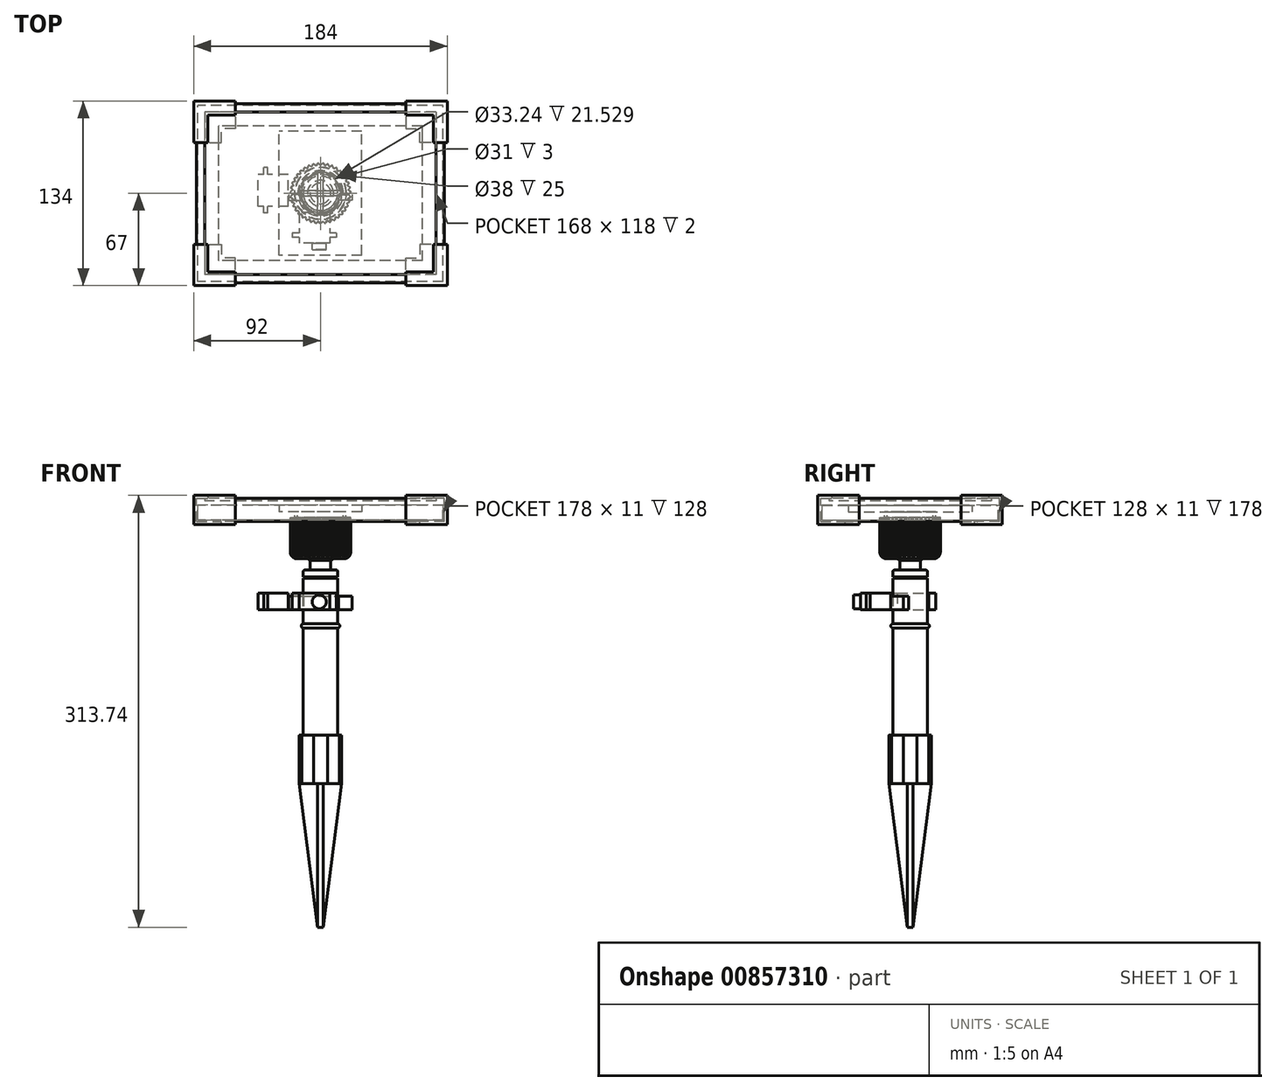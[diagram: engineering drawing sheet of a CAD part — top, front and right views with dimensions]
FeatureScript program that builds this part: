
annotation { "Feature Type Name" : "Feature", "Feature Type Description" : "" }
export const myFeature = defineFeature(function(context is Context, id is Id, definition is map)
    precondition{}
    {
        {
            var Q0;
            Q0=qCreatedBy(makeId("Front.planeOp"),FACE);
            var sketch = newSketch(context, id + "F0", { "sketchPlane" : qUnion([Q0])});
            skArc(sketch, "E0", {"start": v(7.5, 35.85) * mm, "mid": v(14.49, 52.72) * mm, "end": v(0, 63.84) * mm});
            skLineSegment(sketch, "E1", {"start": v(7.5, 35.85) * mm, "end": v(7.5, 28.85) * mm});
            skLineSegment(sketch, "E2", {"start": v(7.5, 28.85) * mm, "end": v(12.5, 28.85) * mm});
            skLineSegment(sketch, "E3", {"start": v(12.5, 28.85) * mm, "end": v(12.5, 23.85) * mm});
            skLineSegment(sketch, "E4", {"start": v(12.5, 23.85) * mm, "end": v(9.5, 23.85) * mm});
            skLineSegment(sketch, "E5", {"start": v(9.5, 23.85) * mm, "end": v(9.5, 22.85) * mm});
            skLineSegment(sketch, "E6", {"start": v(9.5, 22.85) * mm, "end": v(12.5, 22.85) * mm});
            skLineSegment(sketch, "E7", {"start": v(12.5, 22.85) * mm, "end": v(12.5, -10.15) * mm});
            skLineSegment(sketch, "E8", {"start": v(0, -126.15) * mm, "end": v(0, 63.84) * mm});
            skLineSegment(sketch, "E9", {"start": v(12.5, -91.15) * mm, "end": v(14.5, -91.15) * mm});
            skLineSegment(sketch, "E10", {"start": v(14.5, -91.15) * mm, "end": v(14.5, -126.15) * mm});
            skLineSegment(sketch, "E11", {"start": v(14.5, -126.15) * mm, "end": v(0, -126.15) * mm});
            skPoint(sketch, "E12.orphan", {"position": v(0, -41.58) * mm});
            skArc(sketch, "E13", {"start": v(12.5, -13.15) * mm, "mid": v(14, -11.65) * mm, "end": v(12.5, -10.15) * mm});
            skLineSegment(sketch, "E14.trimOffspring", {"start": v(12.5, -13.15) * mm, "end": v(12.5, -91.15) * mm});
            skSolve(sketch);
        }
        {
            var Q0;
            Q0=makeQuery(id+"F0.imprint","IMPRINT",FACE,{"disambiguationData":[TD([[makeQuery(id+"F0.imprint","IMPRINT",EDGE,{"derivedFrom":sQuery(id+"F0.wireOp",EDGE,"E0")}),1.0]])]});
            var Q1;
            Q1=sQuery(id+"F0.wireOp",EDGE,"E8");
            revolve(context, id + "F1", {"surfaceOperationType" : NewSurfaceOperationType.NEW, "entities" : qUnion([Q0]), "axis" : qUnion([Q1]), "revolveType" : RevolveType.FULL});
        }
        {
            var Q0;
            Q0=makeQuery(id+"F1.opRevolve","SWEPT_FACE",FACE,{"disambiguationData":[OSD([sQuery(id+"F0.wireOp",EDGE,"E9")])]});
            var sketch = newSketch(context, id + "F2", { "sketchPlane" : qUnion([Q0])});
            skArc(sketch, "E15", {"start": v(5, 14.61) * mm, "mid": v(0, 15.44) * mm, "end": v(-5, 14.61) * mm});
            skArc(sketch, "E16", {"start": v(5, 13.61) * mm, "mid": v(0, 14.5) * mm, "end": v(-5, 13.61) * mm});
            skLineSegment(sketch, "E17", {"start": v(5, 14.61) * mm, "end": v(5, 13.61) * mm});
            skLineSegment(sketch, "E18.MirrorCS", {"start": v(-5, 14.61) * mm, "end": v(-5, 13.61) * mm});
            skArc(sketch, "E19.1.0", {"start": v(-14.61, 5) * mm, "mid": v(-15.44, 0) * mm, "end": v(-14.61, -5) * mm});
            skArc(sketch, "E19.1.1", {"start": v(-13.61, 5) * mm, "mid": v(-14.5, 0) * mm, "end": v(-13.61, -5) * mm});
            skLineSegment(sketch, "E19.1.2", {"start": v(-14.61, 5) * mm, "end": v(-13.61, 5) * mm});
            skLineSegment(sketch, "E19.1.3", {"start": v(-14.61, -5) * mm, "end": v(-13.61, -5) * mm});
            skArc(sketch, "E19.2.0", {"start": v(-5, -14.61) * mm, "mid": v(0, -15.44) * mm, "end": v(5, -14.61) * mm});
            skArc(sketch, "E19.2.1", {"start": v(-5, -13.61) * mm, "mid": v(0, -14.5) * mm, "end": v(5, -13.61) * mm});
            skLineSegment(sketch, "E19.2.2", {"start": v(-5, -14.61) * mm, "end": v(-5, -13.61) * mm});
            skLineSegment(sketch, "E19.2.3", {"start": v(5, -14.61) * mm, "end": v(5, -13.61) * mm});
            skArc(sketch, "E19.3.0", {"start": v(14.61, -5) * mm, "mid": v(15.44, 0) * mm, "end": v(14.61, 5) * mm});
            skArc(sketch, "E19.3.1", {"start": v(13.61, -5) * mm, "mid": v(14.5, 0) * mm, "end": v(13.61, 5) * mm});
            skLineSegment(sketch, "E19.3.2", {"start": v(14.61, -5) * mm, "end": v(13.61, -5) * mm});
            skLineSegment(sketch, "E19.3.3", {"start": v(14.61, 5) * mm, "end": v(13.61, 5) * mm});
            skSolve(sketch);
        }
        {
            var Q0;
            Q0 = qSketchRegion(id + "F2", true);
            extrude(context, id + "F3", {"entities" : qUnion([Q0]), "operationType" : NewBodyOperationType.ADD, "oppositeDirection" : true, "depth" : 35 * mm, "offsetDistance" : 25 * mm});
        }
        {
            var Q0;
            Q0=qCreatedBy(makeId("Front.planeOp"),FACE);
            var sketch = newSketch(context, id + "F4", { "sketchPlane" : qUnion([Q0])});
            skLineSegment(sketch, "E20", {"start": v(-15.44, -126.15) * mm, "end": v(0, -246.15) * mm});
            skLineSegment(sketch, "E21", {"start": v(0, -246.15) * mm, "end": v(15.44, -126.15) * mm});
            skLineSegment(sketch, "E22", {"start": v(15.44, -126.15) * mm, "end": v(-15.44, -126.15) * mm});
            skSolve(sketch);
        }
        {
            var Q0;
            Q0=makeQuery(id+"F4.imprint","IMPRINT",FACE,{"disambiguationData":[TD([[makeQuery(id+"F4.imprint","IMPRINT",EDGE,{"derivedFrom":sQuery(id+"F4.wireOp",EDGE,"E20")}),1.0]])]});
            extrude(context, id + "F5", {"entities" : qUnion([Q0]), "operationType" : NewBodyOperationType.ADD, "endBound" : BoundingType.SYMMETRIC, "depth" : 4 * mm, "offsetDistance" : 25 * mm});
        }
        {
            var Q0;
            Q0=qCreatedBy(makeId("Right.planeOp"),FACE);
            var sketch = newSketch(context, id + "F6", { "sketchPlane" : qUnion([Q0])});
            skLineSegment(sketch, "E23", {"start": v(15.44, -126.15) * mm, "end": v(0, -246.15) * mm});
            skLineSegment(sketch, "E24", {"start": v(0, -246.15) * mm, "end": v(-15.44, -126.15) * mm});
            skLineSegment(sketch, "E25", {"start": v(-15.44, -126.15) * mm, "end": v(15.44, -126.15) * mm});
            skSolve(sketch);
        }
        {
            var Q0;
            Q0=makeQuery(id+"F6.imprint","IMPRINT",FACE,{"disambiguationData":[TD([[makeQuery(id+"F6.imprint","IMPRINT",EDGE,{"derivedFrom":sQuery(id+"F6.wireOp",EDGE,"E23")}),-1.0]])]});
            extrude(context, id + "F7", {"entities" : qUnion([Q0]), "operationType" : NewBodyOperationType.ADD, "endBound" : BoundingType.SYMMETRIC, "depth" : 4 * mm, "offsetDistance" : 25 * mm});
        }
        {
            var Q0;
            Q0=qCreatedBy(makeId("Right.planeOp"),FACE);
            var sketch = newSketch(context, id + "F8", { "sketchPlane" : qUnion([Q0])});
            skArc(sketch, "E26", {"start": v(0, -232.37) * mm, "mid": v(1.33, -231.87) * mm, "end": v(2, -230.61) * mm});
            skLineSegment(sketch, "E27", {"start": v(0, -232.37) * mm, "end": v(0, -246.15) * mm});
            skLineSegment(sketch, "E28", {"start": v(0, -246.15) * mm, "end": v(7.5, -246.15) * mm});
            skLineSegment(sketch, "E29", {"start": v(2, -230.61) * mm, "end": v(7.5, -230.61) * mm});
            skLineSegment(sketch, "E30", {"start": v(7.5, -230.61) * mm, "end": v(7.5, -246.15) * mm});
            skSolve(sketch);
        }
        {
            var Q0;
            Q0=qCreatedBy(makeId("Right.planeOp"),FACE);
            var sketch = newSketch(context, id + "F9", { "sketchPlane" : qUnion([Q0])});
            skLineSegment(sketch, "E31.bottom", {"start": v(-2, -246.15) * mm, "end": v(2, -246.15) * mm});
            skLineSegment(sketch, "E31.top", {"start": v(-2, -230.61) * mm, "end": v(2, -230.61) * mm});
            skLineSegment(sketch, "E31.left", {"start": v(-2, -246.15) * mm, "end": v(-2, -230.61) * mm});
            skLineSegment(sketch, "E31.right", {"start": v(2, -246.15) * mm, "end": v(2, -230.61) * mm});
            skSolve(sketch);
        }
        {
            var Q0;
            Q0 = qSketchRegion(id + "F9", true);
            extrude(context, id + "F10", {"entities" : qUnion([Q0]), "operationType" : NewBodyOperationType.REMOVE, "endBound" : BoundingType.SYMMETRIC, "oppositeDirection" : true, "depth" : 25 * mm, "offsetDistance" : 25 * mm});
        }
        {
            var Q0;
            Q0=makeQuery(id+"F1.opRevolve","SWEPT_EDGE",EDGE,{"disambiguationData":[OSD([sQuery(id+"F0.wireOp",EDGE,"E2"),sQuery(id+"F0.wireOp",EDGE,"E3")])]});
            fillet(context, id + "F11", {"entities" : qUnion([Q0]), "radius" : 1 * mm, "tangentPropagation" : true, "allowEdgeOverflow" : false});
        }
        {
            var Q0;
            Q0=qCreatedBy(makeId("Front.planeOp"),FACE);
            var sketch = newSketch(context, id + "F12", { "sketchPlane" : qUnion([Q0])});
            skLineSegment(sketch, "E32", {"start": v(-15.5, 37.1) * mm, "end": v(-15.5, 40.1) * mm});
            skLineSegment(sketch, "E33", {"start": v(-15.5, 40.1) * mm, "end": v(-17, 40.1) * mm});
            skLineSegment(sketch, "E34", {"start": v(-15.5, 37.1) * mm, "end": v(-17, 37.1) * mm});
            skArc(sketch, "E35", {"start": v(-22, 42.1) * mm, "mid": v(-20.54, 38.56) * mm, "end": v(-17, 37.1) * mm});
            skArc(sketch, "E36", {"start": v(-19, 42.1) * mm, "mid": v(-18.41, 40.69) * mm, "end": v(-17, 40.1) * mm});
            skLineSegment(sketch, "E37", {"start": v(-19, 42.1) * mm, "end": v(-19, 67.1) * mm});
            skLineSegment(sketch, "E38", {"start": v(-19, 67.1) * mm, "end": v(-22, 67.1) * mm});
            skLineSegment(sketch, "E39", {"start": v(-22, 42.1) * mm, "end": v(-22, 67.1) * mm});
            skSolve(sketch);
        }
        {
            var Q0;
            Q0=makeQuery(id+"F12.imprint","IMPRINT",FACE,{"disambiguationData":[TD([[makeQuery(id+"F12.imprint","IMPRINT",EDGE,{"derivedFrom":sQuery(id+"F12.wireOp",EDGE,"E32")}),1.0]])]});
            var Q1;
            Q1=makeQuery(id+"F1.opRevolve","SWEPT_FACE",FACE,{"disambiguationData":[OSD([sQuery(id+"F0.wireOp",EDGE,"E14.trimOffspring")])]});
            revolve(context, id + "F13", {"surfaceOperationType" : NewSurfaceOperationType.NEW, "entities" : qUnion([Q0]), "axis" : qUnion([Q1]), "revolveType" : RevolveType.FULL});
        }
        {
            var Q0;
            Q0=makeQuery(id+"F13.opRevolve","SWEPT_FACE",FACE,{"disambiguationData":[OSD([sQuery(id+"F12.wireOp",EDGE,"E38")])]});
            var sketch = newSketch(context, id + "F14", { "sketchPlane" : qUnion([Q0])});
            skArc(sketch, "E40", {"start": v(1.59, 21.94) * mm, "mid": v(0, 22) * mm, "end": v(-1.59, 21.94) * mm});
            skLineSegment(sketch, "E41", {"start": v(-1.59, 21.94) * mm, "end": v(0, 20.31) * mm});
            skLineSegment(sketch, "E42.MirrorCS", {"start": v(1.59, 21.94) * mm, "end": v(0, 20.31) * mm});
            skLineSegment(sketch, "E43.1.0", {"start": v(-1.95, 21.91) * mm, "end": v(-3.26, 20.05) * mm});
            skLineSegment(sketch, "E43.1.1", {"start": v(-5.09, 21.4) * mm, "end": v(-3.26, 20.05) * mm});
            skArc(sketch, "E43.1.2", {"start": v(-1.95, 21.91) * mm, "mid": v(-3.53, 21.72) * mm, "end": v(-5.09, 21.4) * mm});
            skLineSegment(sketch, "E44.2.2.0", {"start": v(-5.44, 21.32) * mm, "end": v(-6.43, 19.26) * mm});
            skLineSegment(sketch, "E44.3.2.0", {"start": v(-8.45, 20.31) * mm, "end": v(-6.43, 19.26) * mm});
            skArc(sketch, "E44.6.2.0", {"start": v(-5.44, 21.32) * mm, "mid": v(-6.97, 20.87) * mm, "end": v(-8.45, 20.31) * mm});
            skLineSegment(sketch, "E44.2.3.0", {"start": v(-8.8, 20.17) * mm, "end": v(-9.44, 17.98) * mm});
            skLineSegment(sketch, "E44.3.3.0", {"start": v(-11.6, 18.7) * mm, "end": v(-9.44, 17.98) * mm});
            skArc(sketch, "E44.6.3.0", {"start": v(-8.8, 20.17) * mm, "mid": v(-10.22, 19.48) * mm, "end": v(-11.6, 18.7) * mm});
            skLineSegment(sketch, "E44.2.4.0", {"start": v(-11.91, 18.5) * mm, "end": v(-12.2, 16.24) * mm});
            skLineSegment(sketch, "E44.3.4.0", {"start": v(-14.45, 16.59) * mm, "end": v(-12.2, 16.24) * mm});
            skArc(sketch, "E44.6.4.0", {"start": v(-11.91, 18.5) * mm, "mid": v(-13.22, 17.59) * mm, "end": v(-14.45, 16.59) * mm});
            skLineSegment(sketch, "E44.2.5.0", {"start": v(-14.73, 16.34) * mm, "end": v(-14.65, 14.07) * mm});
            skLineSegment(sketch, "E44.3.5.0", {"start": v(-16.92, 14.06) * mm, "end": v(-14.65, 14.07) * mm});
            skArc(sketch, "E44.6.5.0", {"start": v(-14.73, 16.34) * mm, "mid": v(-15.87, 15.24) * mm, "end": v(-16.92, 14.06) * mm});
            skLineSegment(sketch, "E44.2.6.0", {"start": v(-17.16, 13.77) * mm, "end": v(-16.71, 11.54) * mm});
            skLineSegment(sketch, "E44.3.6.0", {"start": v(-18.96, 11.16) * mm, "end": v(-16.71, 11.54) * mm});
            skArc(sketch, "E44.6.6.0", {"start": v(-17.16, 13.77) * mm, "mid": v(-18.1, 12.5) * mm, "end": v(-18.96, 11.16) * mm});
            skLineSegment(sketch, "E44.2.7.0", {"start": v(-19.14, 10.84) * mm, "end": v(-18.35, 8.7) * mm});
            skLineSegment(sketch, "E44.3.7.0", {"start": v(-20.5, 7.97) * mm, "end": v(-18.35, 8.7) * mm});
            skArc(sketch, "E44.6.7.0", {"start": v(-19.14, 10.84) * mm, "mid": v(-19.88, 9.43) * mm, "end": v(-20.5, 7.97) * mm});
            skLineSegment(sketch, "E44.2.8.0", {"start": v(-20.64, 7.63) * mm, "end": v(-19.5, 5.65) * mm});
            skLineSegment(sketch, "E44.3.8.0", {"start": v(-21.52, 4.58) * mm, "end": v(-19.5, 5.65) * mm});
            skArc(sketch, "E44.6.8.0", {"start": v(-20.64, 7.63) * mm, "mid": v(-21.13, 6.12) * mm, "end": v(-21.52, 4.58) * mm});
            skLineSegment(sketch, "E44.2.9.0", {"start": v(-21.6, 4.22) * mm, "end": v(-20.16, 2.45) * mm});
            skLineSegment(sketch, "E44.3.9.0", {"start": v(-21.97, 1.07) * mm, "end": v(-20.16, 2.45) * mm});
            skArc(sketch, "E44.6.9.0", {"start": v(-21.6, 4.22) * mm, "mid": v(-21.84, 2.65) * mm, "end": v(-21.97, 1.07) * mm});
            skLineSegment(sketch, "E44.2.10.0", {"start": v(-21.99, 0.7) * mm, "end": v(-20.3, -0.82) * mm});
            skLineSegment(sketch, "E44.3.10.0", {"start": v(-21.86, -2.47) * mm, "end": v(-20.3, -0.82) * mm});
            skArc(sketch, "E44.6.10.0", {"start": v(-21.99, 0.7) * mm, "mid": v(-21.98, -0.89) * mm, "end": v(-21.86, -2.47) * mm});
            skLineSegment(sketch, "E44.2.11.0", {"start": v(-21.82, -2.84) * mm, "end": v(-19.9, -4.06) * mm});
            skLineSegment(sketch, "E44.3.11.0", {"start": v(-21.18, -5.94) * mm, "end": v(-19.9, -4.06) * mm});
            skArc(sketch, "E44.6.11.0", {"start": v(-21.82, -2.84) * mm, "mid": v(-21.56, -4.4) * mm, "end": v(-21.18, -5.94) * mm});
            skLineSegment(sketch, "E44.2.12.0", {"start": v(-21.08, -6.3) * mm, "end": v(-19, -7.2) * mm});
            skLineSegment(sketch, "E44.3.12.0", {"start": v(-19.95, -9.26) * mm, "end": v(-19, -7.2) * mm});
            skArc(sketch, "E44.6.12.0", {"start": v(-21.08, -6.3) * mm, "mid": v(-20.57, -7.8) * mm, "end": v(-19.95, -9.26) * mm});
            skLineSegment(sketch, "E44.2.13.0", {"start": v(-19.8, -9.6) * mm, "end": v(-17.59, -10.16) * mm});
            skLineSegment(sketch, "E44.3.13.0", {"start": v(-18.2, -12.34) * mm, "end": v(-17.59, -10.16) * mm});
            skArc(sketch, "E44.6.13.0", {"start": v(-19.8, -9.6) * mm, "mid": v(-19.05, -11) * mm, "end": v(-18.2, -12.34) * mm});
            skLineSegment(sketch, "E44.2.14.0", {"start": v(-18, -12.65) * mm, "end": v(-15.73, -12.85) * mm});
            skLineSegment(sketch, "E44.3.14.0", {"start": v(-16, -15.1) * mm, "end": v(-15.73, -12.85) * mm});
            skArc(sketch, "E44.6.14.0", {"start": v(-18, -12.65) * mm, "mid": v(-17.04, -13.91) * mm, "end": v(-16, -15.1) * mm});
            skLineSegment(sketch, "E44.2.15.0", {"start": v(-15.74, -15.37) * mm, "end": v(-13.47, -15.2) * mm});
            skLineSegment(sketch, "E44.3.15.0", {"start": v(-13.36, -17.48) * mm, "end": v(-13.47, -15.2) * mm});
            skArc(sketch, "E44.6.15.0", {"start": v(-15.74, -15.37) * mm, "mid": v(-14.59, -16.47) * mm, "end": v(-13.36, -17.48) * mm});
            skLineSegment(sketch, "E44.2.16.0", {"start": v(-13.07, -17.7) * mm, "end": v(-10.86, -17.17) * mm});
            skLineSegment(sketch, "E44.3.16.0", {"start": v(-10.39, -19.4) * mm, "end": v(-10.86, -17.17) * mm});
            skArc(sketch, "E44.6.16.0", {"start": v(-13.07, -17.7) * mm, "mid": v(-11.76, -18.6) * mm, "end": v(-10.39, -19.4) * mm});
            skLineSegment(sketch, "E44.2.17.0", {"start": v(-10.06, -19.57) * mm, "end": v(-7.96, -18.68) * mm});
            skLineSegment(sketch, "E44.3.17.0", {"start": v(-7.14, -20.8) * mm, "end": v(-7.96, -18.68) * mm});
            skArc(sketch, "E44.6.17.0", {"start": v(-10.06, -19.57) * mm, "mid": v(-8.62, -20.24) * mm, "end": v(-7.14, -20.8) * mm});
            skLineSegment(sketch, "E44.2.18.0", {"start": v(-6.8, -20.93) * mm, "end": v(-4.86, -19.72) * mm});
            skLineSegment(sketch, "E44.3.18.0", {"start": v(-3.71, -21.68) * mm, "end": v(-4.86, -19.72) * mm});
            skArc(sketch, "E44.6.18.0", {"start": v(-6.8, -20.93) * mm, "mid": v(-5.26, -21.36) * mm, "end": v(-3.71, -21.68) * mm});
            skLineSegment(sketch, "E44.2.19.0", {"start": v(-3.35, -21.74) * mm, "end": v(-1.63, -20.24) * mm});
            skLineSegment(sketch, "E44.3.19.0", {"start": v(-0.18, -22) * mm, "end": v(-1.63, -20.24) * mm});
            skArc(sketch, "E44.6.19.0", {"start": v(-3.35, -21.74) * mm, "mid": v(-1.77, -21.93) * mm, "end": v(-0.18, -22) * mm});
            skLineSegment(sketch, "E45.2.20.0", {"start": v(0.18, -22) * mm, "end": v(1.63, -20.24) * mm});
            skLineSegment(sketch, "E45.3.20.0", {"start": v(3.35, -21.74) * mm, "end": v(1.63, -20.24) * mm});
            skArc(sketch, "E45.6.20.0", {"start": v(0.18, -22) * mm, "mid": v(1.77, -21.93) * mm, "end": v(3.35, -21.74) * mm});
            skLineSegment(sketch, "E45.2.21.0", {"start": v(3.71, -21.68) * mm, "end": v(4.86, -19.72) * mm});
            skLineSegment(sketch, "E45.3.21.0", {"start": v(6.8, -20.93) * mm, "end": v(4.86, -19.72) * mm});
            skArc(sketch, "E45.6.21.0", {"start": v(3.71, -21.68) * mm, "mid": v(5.26, -21.36) * mm, "end": v(6.8, -20.93) * mm});
            skLineSegment(sketch, "E45.2.22.0", {"start": v(7.14, -20.8) * mm, "end": v(7.96, -18.68) * mm});
            skLineSegment(sketch, "E45.3.22.0", {"start": v(10.06, -19.57) * mm, "end": v(7.96, -18.68) * mm});
            skArc(sketch, "E45.6.22.0", {"start": v(7.14, -20.8) * mm, "mid": v(8.62, -20.24) * mm, "end": v(10.06, -19.57) * mm});
            skLineSegment(sketch, "E45.2.23.0", {"start": v(10.39, -19.4) * mm, "end": v(10.86, -17.17) * mm});
            skLineSegment(sketch, "E45.3.23.0", {"start": v(13.07, -17.7) * mm, "end": v(10.86, -17.17) * mm});
            skArc(sketch, "E45.6.23.0", {"start": v(10.39, -19.4) * mm, "mid": v(11.76, -18.6) * mm, "end": v(13.07, -17.7) * mm});
            skLineSegment(sketch, "E45.2.24.0", {"start": v(13.36, -17.48) * mm, "end": v(13.47, -15.2) * mm});
            skLineSegment(sketch, "E45.3.24.0", {"start": v(15.74, -15.37) * mm, "end": v(13.47, -15.2) * mm});
            skArc(sketch, "E45.6.24.0", {"start": v(13.36, -17.48) * mm, "mid": v(14.59, -16.47) * mm, "end": v(15.74, -15.37) * mm});
            skLineSegment(sketch, "E45.2.25.0", {"start": v(16, -15.1) * mm, "end": v(15.73, -12.85) * mm});
            skLineSegment(sketch, "E45.3.25.0", {"start": v(18, -12.65) * mm, "end": v(15.73, -12.85) * mm});
            skArc(sketch, "E45.6.25.0", {"start": v(16, -15.1) * mm, "mid": v(17.04, -13.91) * mm, "end": v(18, -12.65) * mm});
            skLineSegment(sketch, "E45.2.26.0", {"start": v(18.2, -12.34) * mm, "end": v(17.59, -10.16) * mm});
            skLineSegment(sketch, "E45.3.26.0", {"start": v(19.8, -9.6) * mm, "end": v(17.59, -10.16) * mm});
            skArc(sketch, "E45.6.26.0", {"start": v(18.2, -12.34) * mm, "mid": v(19.05, -11) * mm, "end": v(19.8, -9.6) * mm});
            skLineSegment(sketch, "E45.2.27.0", {"start": v(19.95, -9.26) * mm, "end": v(19, -7.2) * mm});
            skLineSegment(sketch, "E45.3.27.0", {"start": v(21.08, -6.3) * mm, "end": v(19, -7.2) * mm});
            skArc(sketch, "E45.6.27.0", {"start": v(19.95, -9.26) * mm, "mid": v(20.57, -7.8) * mm, "end": v(21.08, -6.3) * mm});
            skLineSegment(sketch, "E45.2.28.0", {"start": v(21.18, -5.94) * mm, "end": v(19.9, -4.06) * mm});
            skLineSegment(sketch, "E45.3.28.0", {"start": v(21.82, -2.84) * mm, "end": v(19.9, -4.06) * mm});
            skArc(sketch, "E45.6.28.0", {"start": v(21.18, -5.94) * mm, "mid": v(21.56, -4.4) * mm, "end": v(21.82, -2.84) * mm});
            skLineSegment(sketch, "E45.2.29.0", {"start": v(21.86, -2.47) * mm, "end": v(20.3, -0.82) * mm});
            skLineSegment(sketch, "E45.3.29.0", {"start": v(21.99, 0.7) * mm, "end": v(20.3, -0.82) * mm});
            skArc(sketch, "E45.6.29.0", {"start": v(21.86, -2.47) * mm, "mid": v(21.98, -0.89) * mm, "end": v(21.99, 0.7) * mm});
            skLineSegment(sketch, "E45.2.30.0", {"start": v(21.97, 1.07) * mm, "end": v(20.16, 2.45) * mm});
            skLineSegment(sketch, "E45.3.30.0", {"start": v(21.6, 4.22) * mm, "end": v(20.16, 2.45) * mm});
            skArc(sketch, "E45.6.30.0", {"start": v(21.97, 1.07) * mm, "mid": v(21.84, 2.65) * mm, "end": v(21.6, 4.22) * mm});
            skLineSegment(sketch, "E45.2.31.0", {"start": v(21.52, 4.58) * mm, "end": v(19.5, 5.65) * mm});
            skLineSegment(sketch, "E45.3.31.0", {"start": v(20.64, 7.63) * mm, "end": v(19.5, 5.65) * mm});
            skArc(sketch, "E45.6.31.0", {"start": v(21.52, 4.58) * mm, "mid": v(21.13, 6.12) * mm, "end": v(20.64, 7.63) * mm});
            skLineSegment(sketch, "E45.2.32.0", {"start": v(20.5, 7.97) * mm, "end": v(18.35, 8.7) * mm});
            skLineSegment(sketch, "E45.3.32.0", {"start": v(19.14, 10.84) * mm, "end": v(18.35, 8.7) * mm});
            skArc(sketch, "E45.6.32.0", {"start": v(20.5, 7.97) * mm, "mid": v(19.88, 9.43) * mm, "end": v(19.14, 10.84) * mm});
            skLineSegment(sketch, "E45.2.33.0", {"start": v(18.96, 11.16) * mm, "end": v(16.71, 11.54) * mm});
            skLineSegment(sketch, "E45.3.33.0", {"start": v(17.16, 13.77) * mm, "end": v(16.71, 11.54) * mm});
            skArc(sketch, "E45.6.33.0", {"start": v(18.96, 11.16) * mm, "mid": v(18.1, 12.5) * mm, "end": v(17.16, 13.77) * mm});
            skLineSegment(sketch, "E45.2.34.0", {"start": v(16.92, 14.06) * mm, "end": v(14.65, 14.07) * mm});
            skLineSegment(sketch, "E45.3.34.0", {"start": v(14.73, 16.34) * mm, "end": v(14.65, 14.07) * mm});
            skArc(sketch, "E45.6.34.0", {"start": v(16.92, 14.06) * mm, "mid": v(15.87, 15.24) * mm, "end": v(14.73, 16.34) * mm});
            skLineSegment(sketch, "E45.2.35.0", {"start": v(14.45, 16.59) * mm, "end": v(12.2, 16.24) * mm});
            skLineSegment(sketch, "E45.3.35.0", {"start": v(11.91, 18.5) * mm, "end": v(12.2, 16.24) * mm});
            skArc(sketch, "E45.6.35.0", {"start": v(14.45, 16.59) * mm, "mid": v(13.22, 17.59) * mm, "end": v(11.91, 18.5) * mm});
            skLineSegment(sketch, "E45.2.36.0", {"start": v(11.6, 18.7) * mm, "end": v(9.44, 17.98) * mm});
            skLineSegment(sketch, "E45.3.36.0", {"start": v(8.8, 20.17) * mm, "end": v(9.44, 17.98) * mm});
            skArc(sketch, "E45.6.36.0", {"start": v(11.6, 18.7) * mm, "mid": v(10.22, 19.48) * mm, "end": v(8.8, 20.17) * mm});
            skLineSegment(sketch, "E45.2.37.0", {"start": v(8.45, 20.31) * mm, "end": v(6.43, 19.26) * mm});
            skLineSegment(sketch, "E45.3.37.0", {"start": v(5.44, 21.32) * mm, "end": v(6.43, 19.26) * mm});
            skArc(sketch, "E45.6.37.0", {"start": v(8.45, 20.31) * mm, "mid": v(6.97, 20.87) * mm, "end": v(5.44, 21.32) * mm});
            skLineSegment(sketch, "E45.2.38.0", {"start": v(5.09, 21.4) * mm, "end": v(3.26, 20.05) * mm});
            skLineSegment(sketch, "E45.3.38.0", {"start": v(1.95, 21.91) * mm, "end": v(3.26, 20.05) * mm});
            skArc(sketch, "E45.6.38.0", {"start": v(5.09, 21.4) * mm, "mid": v(3.53, 21.72) * mm, "end": v(1.95, 21.91) * mm});
            skSolve(sketch);
        }
        {
            var Q0;
            Q0 = qSketchRegion(id + "F14", true);
            extrude(context, id + "F15", {"entities" : qUnion([Q0]), "operationType" : NewBodyOperationType.REMOVE, "endBound" : BoundingType.THROUGH_ALL, "oppositeDirection" : true, "depth" : 25 * mm, "offsetDistance" : 25 * mm});
        }
        {
            var Q0;
            Q0=qCreatedBy(makeId("Front.planeOp"),FACE);
            var sketch = newSketch(context, id + "F16", { "sketchPlane" : qUnion([Q0])});
            skLineSegment(sketch, "E46", {"start": v(-18.62, 49.6) * mm, "end": v(-18.62, 71.13) * mm});
            skLineSegment(sketch, "E47", {"start": v(-18.62, 71.13) * mm, "end": v(-16.62, 71.13) * mm});
            skLineSegment(sketch, "E48", {"start": v(-16.62, 71.13) * mm, "end": v(-16.62, 49.6) * mm});
            skLineSegment(sketch, "E49", {"start": v(-18.62, 49.6) * mm, "end": v(-16.62, 49.6) * mm});
            skSolve(sketch);
        }
        {
            var Q0;
            Q0=makeQuery(id+"F16.imprint","IMPRINT",FACE,{"disambiguationData":[TD([[makeQuery(id+"F16.imprint","IMPRINT",EDGE,{"derivedFrom":sQuery(id+"F16.wireOp",EDGE,"E46")}),-1.0]])]});
            var Q1;
            Q1=makeQuery(id+"F1.opRevolve","SWEPT_FACE",FACE,{"disambiguationData":[OSD([sQuery(id+"F0.wireOp",EDGE,"E7")])]});
            revolve(context, id + "F17", {"surfaceOperationType" : NewSurfaceOperationType.NEW, "entities" : qUnion([Q0]), "axis" : qUnion([Q1]), "revolveType" : RevolveType.FULL});
        }
        {
            var Q0;
            Q0=makeQuery(id+"F17.opRevolve","SWEPT_FACE",FACE,{"disambiguationData":[OSD([sQuery(id+"F16.wireOp",EDGE,"E47")])]});
            var sketch = newSketch(context, id + "F18", { "sketchPlane" : qUnion([Q0])});
            skLineSegment(sketch, "E50.bottom", {"start": v(30, -45) * mm, "end": v(-30, -45) * mm});
            skLineSegment(sketch, "E50.top", {"start": v(30, 45) * mm, "end": v(-30, 45) * mm});
            skLineSegment(sketch, "E50.left", {"start": v(30, -45) * mm, "end": v(30, 45) * mm});
            skLineSegment(sketch, "E50.right", {"start": v(-30, -45) * mm, "end": v(-30, 45) * mm});
            skPoint(sketch, "E50.middle", {"position": v(0, 0) * mm});
            skSolve(sketch);
        }
        {
            var Q0;
            Q0 = qSketchRegion(id + "F18", true);
            extrude(context, id + "F19", {"entities" : qUnion([Q0]), "operationType" : NewBodyOperationType.ADD, "depth" : 5 * mm, "offsetDistance" : 25 * mm});
        }
        {
            var Q0;
            Q0=makeQuery(id+"F19.opExtrude","CAP_FACE",FACE,{"disambiguationData":[OSD([sQuery(id+"F18.wireOp",EDGE,"E50.bottom"),sQuery(id+"F18.wireOp",EDGE,"E50.top"),sQuery(id+"F18.wireOp",EDGE,"E50.left"),sQuery(id+"F18.wireOp",EDGE,"E50.right")])],"isStart":false});
            var sketch = newSketch(context, id + "F20", { "sketchPlane" : qUnion([Q0])});
            skLineSegment(sketch, "E51.bottom", {"start": v(-90, -65) * mm, "end": v(90, -65) * mm});
            skLineSegment(sketch, "E51.top", {"start": v(-90, 65) * mm, "end": v(90, 65) * mm});
            skLineSegment(sketch, "E51.left", {"start": v(-90, -65) * mm, "end": v(-90, 65) * mm});
            skLineSegment(sketch, "E51.right", {"start": v(90, -65) * mm, "end": v(90, 65) * mm});
            skPoint(sketch, "E51.middle", {"position": v(0, 0) * mm});
            skSolve(sketch);
        }
        {
            var Q0;
            Q0 = qSketchRegion(id + "F20", true);
            extrude(context, id + "F21", {"entities" : qUnion([Q0]), "operationType" : NewBodyOperationType.ADD, "depth" : 3 * mm, "offsetDistance" : 25 * mm});
        }
        {
            var Q0;
            Q0=makeQuery(id+"F21.opExtrude","CAP_FACE",FACE,{"disambiguationData":[OSD([sQuery(id+"F20.wireOp",EDGE,"E51.bottom"),sQuery(id+"F20.wireOp",EDGE,"E51.top"),sQuery(id+"F20.wireOp",EDGE,"E51.left"),sQuery(id+"F20.wireOp",EDGE,"E51.right")])],"isStart":false});
            var sketch = newSketch(context, id + "F22", { "sketchPlane" : qUnion([Q0])});
            skLineSegment(sketch, "E52.bottom", {"start": v(90, 65) * mm, "end": v(-90, 65) * mm});
            skLineSegment(sketch, "E52.top", {"start": v(90, -65) * mm, "end": v(-90, -65) * mm});
            skLineSegment(sketch, "E52.left", {"start": v(90, 65) * mm, "end": v(90, -65) * mm});
            skLineSegment(sketch, "E52.right", {"start": v(-90, 65) * mm, "end": v(-90, -65) * mm});
            skPoint(sketch, "E52.middle", {"position": v(0, 0) * mm});
            skLineSegment(sketch, "E53.bottom", {"start": v(84, 59) * mm, "end": v(-84, 59) * mm});
            skLineSegment(sketch, "E53.top", {"start": v(84, -59) * mm, "end": v(-84, -59) * mm});
            skLineSegment(sketch, "E53.left", {"start": v(84, 59) * mm, "end": v(84, -59) * mm});
            skLineSegment(sketch, "E53.right", {"start": v(-84, 59) * mm, "end": v(-84, -59) * mm});
            skSolve(sketch);
        }
        {
            var Q0;
            Q0 = qSketchRegion(id + "F22", true);
            extrude(context, id + "F23", {"entities" : qUnion([Q0]), "operationType" : NewBodyOperationType.ADD, "depth" : 2 * mm, "offsetDistance" : 25 * mm});
        }
        {
            var Q0;
            Q0=makeQuery(id+"F21.opExtrude","CAP_FACE",FACE,{"disambiguationData":[OSD([sQuery(id+"F20.wireOp",EDGE,"E51.bottom"),sQuery(id+"F20.wireOp",EDGE,"E51.top"),sQuery(id+"F20.wireOp",EDGE,"E51.left"),sQuery(id+"F20.wireOp",EDGE,"E51.right")])],"isStart":true});
            var sketch = newSketch(context, id + "F24", { "sketchPlane" : qUnion([Q0])});
            skLineSegment(sketch, "E54.bottom", {"start": v(90, 65) * mm, "end": v(-90, 65) * mm});
            skLineSegment(sketch, "E54.top", {"start": v(90, -65) * mm, "end": v(-90, -65) * mm});
            skLineSegment(sketch, "E54.left", {"start": v(90, 65) * mm, "end": v(90, -65) * mm});
            skLineSegment(sketch, "E54.right", {"start": v(-90, 65) * mm, "end": v(-90, -65) * mm});
            skPoint(sketch, "E54.middle", {"position": v(0, 0) * mm});
            skLineSegment(sketch, "E55.bottom", {"start": v(89, 64) * mm, "end": v(-89, 64) * mm});
            skLineSegment(sketch, "E55.top", {"start": v(89, -64) * mm, "end": v(-89, -64) * mm});
            skLineSegment(sketch, "E55.left", {"start": v(89, 64) * mm, "end": v(89, -64) * mm});
            skLineSegment(sketch, "E55.right", {"start": v(-89, 64) * mm, "end": v(-89, -64) * mm});
            skSolve(sketch);
        }
        {
            var Q0;
            Q0 = qSketchRegion(id + "F24", true);
            extrude(context, id + "F25", {"entities" : qUnion([Q0]), "operationType" : NewBodyOperationType.ADD, "depth" : 11 * mm, "offsetDistance" : 25 * mm});
        }
        {
            var Q0;
            Q0=makeQuery(id+"F25.opExtrude","CAP_FACE",FACE,{"disambiguationData":[OSD([sQuery(id+"F24.wireOp",EDGE,"E54.bottom"),sQuery(id+"F24.wireOp",EDGE,"E54.top"),sQuery(id+"F24.wireOp",EDGE,"E54.left"),sQuery(id+"F24.wireOp",EDGE,"E54.right"),sQuery(id+"F24.wireOp",EDGE,"E55.bottom"),sQuery(id+"F24.wireOp",EDGE,"E55.top"),sQuery(id+"F24.wireOp",EDGE,"E55.left"),sQuery(id+"F24.wireOp",EDGE,"E55.right")])],"isStart":false});
            var sketch = newSketch(context, id + "F26", { "sketchPlane" : qUnion([Q0])});
            skLineSegment(sketch, "E56.bottom", {"start": v(90, 65) * mm, "end": v(-90, 65) * mm});
            skLineSegment(sketch, "E56.top", {"start": v(90, -65) * mm, "end": v(-90, -65) * mm});
            skLineSegment(sketch, "E56.left", {"start": v(90, 65) * mm, "end": v(90, -65) * mm});
            skLineSegment(sketch, "E56.right", {"start": v(-90, 65) * mm, "end": v(-90, -65) * mm});
            skPoint(sketch, "E56.middle", {"position": v(0, 0) * mm});
            skLineSegment(sketch, "E57.bottom", {"start": v(74, 49) * mm, "end": v(-74, 49) * mm});
            skLineSegment(sketch, "E57.top", {"start": v(74, -49) * mm, "end": v(-74, -49) * mm});
            skLineSegment(sketch, "E57.left", {"start": v(74, 49) * mm, "end": v(74, -49) * mm});
            skLineSegment(sketch, "E57.right", {"start": v(-74, 49) * mm, "end": v(-74, -49) * mm});
            skSolve(sketch);
        }
        {
            var Q0;
            Q0 = qSketchRegion(id + "F26", true);
            extrude(context, id + "F27", {"entities" : qUnion([Q0]), "operationType" : NewBodyOperationType.ADD, "depth" : 1 * mm, "offsetDistance" : 25 * mm});
        }
        {
            var Q0;
            Q0=makeQuery(id+"F23.opExtrude","CAP_FACE",FACE,{"disambiguationData":[OSD([sQuery(id+"F22.wireOp",EDGE,"E52.bottom"),sQuery(id+"F22.wireOp",EDGE,"E52.top"),sQuery(id+"F22.wireOp",EDGE,"E52.left"),sQuery(id+"F22.wireOp",EDGE,"E52.right"),sQuery(id+"F22.wireOp",EDGE,"E53.bottom"),sQuery(id+"F22.wireOp",EDGE,"E53.top"),sQuery(id+"F22.wireOp",EDGE,"E53.left"),sQuery(id+"F22.wireOp",EDGE,"E53.right")])],"isStart":false});
            var sketch = newSketch(context, id + "F28", { "sketchPlane" : qUnion([Q0])});
            skLineSegment(sketch, "E58.bottom", {"start": v(92, -67) * mm, "end": v(62, -67) * mm});
            skLineSegment(sketch, "E58.top", {"start": v(92, -37) * mm, "end": v(82, -37) * mm});
            skLineSegment(sketch, "E58.left", {"start": v(92, -67) * mm, "end": v(92, -37) * mm});
            skLineSegment(sketch, "E58.right", {"start": v(62, -67) * mm, "end": v(62, -57) * mm});
            skLineSegment(sketch, "E59.top", {"start": v(62, -57) * mm, "end": v(82, -57) * mm});
            skLineSegment(sketch, "E59.right", {"start": v(82, -37) * mm, "end": v(82, -57) * mm});
            skLineSegment(sketch, "E60.MirrorCS", {"start": v(-82, -37) * mm, "end": v(-82, -57) * mm});
            skLineSegment(sketch, "E61.MirrorCS", {"start": v(-92, -37) * mm, "end": v(-82, -37) * mm});
            skLineSegment(sketch, "E62.MirrorCS", {"start": v(-92, -67) * mm, "end": v(-92, -37) * mm});
            skLineSegment(sketch, "E63.MirrorCS", {"start": v(-92, -67) * mm, "end": v(-62, -67) * mm});
            skLineSegment(sketch, "E64.MirrorCS", {"start": v(-62, -67) * mm, "end": v(-62, -57) * mm});
            skLineSegment(sketch, "E65.MirrorCS", {"start": v(-62, -57) * mm, "end": v(-82, -57) * mm});
            skLineSegment(sketch, "E66.MirrorCS", {"start": v(-92, 37) * mm, "end": v(-82, 37) * mm});
            skLineSegment(sketch, "E67.MirrorCS", {"start": v(-82, 37) * mm, "end": v(-82, 57) * mm});
            skLineSegment(sketch, "E68.MirrorCS", {"start": v(-62, 57) * mm, "end": v(-82, 57) * mm});
            skLineSegment(sketch, "E69.MirrorCS", {"start": v(-62, 67) * mm, "end": v(-62, 57) * mm});
            skLineSegment(sketch, "E70.MirrorCS", {"start": v(-92, 67) * mm, "end": v(-62, 67) * mm});
            skLineSegment(sketch, "E71.MirrorCS", {"start": v(-92, 67) * mm, "end": v(-92, 37) * mm});
            skLineSegment(sketch, "E72.MirrorCS", {"start": v(62, 67) * mm, "end": v(62, 57) * mm});
            skLineSegment(sketch, "E73.MirrorCS", {"start": v(62, 57) * mm, "end": v(82, 57) * mm});
            skLineSegment(sketch, "E74.MirrorCS", {"start": v(82, 37) * mm, "end": v(82, 57) * mm});
            skLineSegment(sketch, "E75.MirrorCS", {"start": v(92, 37) * mm, "end": v(82, 37) * mm});
            skLineSegment(sketch, "E76.MirrorCS", {"start": v(92, 67) * mm, "end": v(92, 37) * mm});
            skLineSegment(sketch, "E77.MirrorCS", {"start": v(92, 67) * mm, "end": v(62, 67) * mm});
            skSolve(sketch);
        }
        {
            var Q0;
            Q0 = qSketchRegion(id + "F28", true);
            extrude(context, id + "F29", {"entities" : qUnion([Q0]), "operationType" : NewBodyOperationType.ADD, "depth" : 2 * mm, "offsetDistance" : 25 * mm});
        }
        {
            var Q0;
            {var subQ0=sQuery(id+"F28.wireOp",EDGE,"E61.MirrorCS");var subQ2=sQuery(id+"F28.wireOp",EDGE,"E62.MirrorCS");var subQ4=sQuery(id+"F28.wireOp",EDGE,"E63.MirrorCS");var subQ5=sQuery(id+"F28.wireOp",EDGE,"E64.MirrorCS");Q0=makeQuery(id+"F29.boolean.opBoolean","SPLIT",FACE,{"disambiguationData":[TD([makeQuery(id+"F21.opExtrude","SWEPT_FACE",FACE,{"disambiguationData":[OSD([sQuery(id+"F20.wireOp",EDGE,"E51.bottom")])]})])],"derivedFrom":makeQuery(id+"F29.opExtrude","CAP_FACE",FACE,{"disambiguationData":[OSD([sQuery(id+"F28.wireOp",EDGE,"E60.MirrorCS"),subQ0,subQ2,subQ4,subQ5,sQuery(id+"F28.wireOp",EDGE,"E65.MirrorCS")])],"isStart":true})});}
            var sketch = newSketch(context, id + "F30", { "sketchPlane" : qUnion([Q0])});
            skLineSegment(sketch, "E78", {"start": v(-62, 67) * mm, "end": v(-62, 65) * mm});
            skLineSegment(sketch, "E79", {"start": v(-62, 65) * mm, "end": v(-90, 65) * mm});
            skLineSegment(sketch, "E80", {"start": v(-90, 65) * mm, "end": v(-90, 37) * mm});
            skLineSegment(sketch, "E81", {"start": v(-90, 37) * mm, "end": v(-92, 37) * mm});
            skLineSegment(sketch, "E82", {"start": v(-92, 37) * mm, "end": v(-92, 67) * mm});
            skLineSegment(sketch, "E83", {"start": v(-92, 67) * mm, "end": v(-62, 67) * mm});
            skLineSegment(sketch, "E84", {"start": v(-62, -67) * mm, "end": v(-92, -67) * mm});
            skLineSegment(sketch, "E85", {"start": v(-92, -67) * mm, "end": v(-92, -37) * mm});
            skLineSegment(sketch, "E86", {"start": v(-92, -37) * mm, "end": v(-90, -37) * mm});
            skLineSegment(sketch, "E87", {"start": v(-90, -37) * mm, "end": v(-90, -64.98) * mm});
            skLineSegment(sketch, "E88", {"start": v(-90, -64.98) * mm, "end": v(-62, -64.98) * mm});
            skLineSegment(sketch, "E89", {"start": v(-62, -64.98) * mm, "end": v(-62, -67) * mm});
            skLineSegment(sketch, "E90", {"start": v(90, -37) * mm, "end": v(92, -37) * mm});
            skLineSegment(sketch, "E91", {"start": v(92, -37) * mm, "end": v(92, -67) * mm});
            skLineSegment(sketch, "E92", {"start": v(92, -67) * mm, "end": v(62, -67) * mm});
            skLineSegment(sketch, "E93", {"start": v(62, -67) * mm, "end": v(62, -65) * mm});
            skLineSegment(sketch, "E94", {"start": v(62, -65) * mm, "end": v(90, -65) * mm});
            skLineSegment(sketch, "E95", {"start": v(90, -65) * mm, "end": v(90, -37) * mm});
            skLineSegment(sketch, "E96", {"start": v(92, 67) * mm, "end": v(92, 37) * mm});
            skLineSegment(sketch, "E97", {"start": v(92, 37) * mm, "end": v(90, 37) * mm});
            skLineSegment(sketch, "E98", {"start": v(90, 37) * mm, "end": v(90, 65) * mm});
            skLineSegment(sketch, "E99", {"start": v(90, 65) * mm, "end": v(62, 65) * mm});
            skLineSegment(sketch, "E100", {"start": v(62, 65) * mm, "end": v(62, 67) * mm});
            skLineSegment(sketch, "E101", {"start": v(62, 67) * mm, "end": v(92, 67) * mm});
            skSolve(sketch);
        }
        {
            var Q0;
            Q0 = qSketchRegion(id + "F30", true);
            var Q1;
            Q1=makeQuery(id+"F27.opExtrude","CAP_VERTEX",VERTEX,{"disambiguationData":[OSD([sQuery(id+"F26.wireOp",EDGE,"E56.bottom"),sQuery(id+"F26.wireOp",EDGE,"E56.right")])],"isStart":false});
            extrude(context, id + "F31", {"entities" : qUnion([Q0]), "operationType" : NewBodyOperationType.ADD, "endBound" : BoundingType.UP_TO_VERTEX, "depth" : 25 * mm, "endBoundEntityVertex" : qUnion([Q1]), "offsetDistance" : 25 * mm});
        }
        {
            var Q0;
            {var subQ0=dummyQuery(id+"F31.vertexPlane.planeOp",FACE);Q0=makeQuery(id+"F31.boolean.opBoolean","MERGE",FACE,{"derivedFrom":[makeQuery(id+"F27.opExtrude","CAP_FACE",FACE,{"disambiguationData":[OSD([sQuery(id+"F26.wireOp",EDGE,"E56.bottom"),sQuery(id+"F26.wireOp",EDGE,"E56.top"),sQuery(id+"F26.wireOp",EDGE,"E56.left"),sQuery(id+"F26.wireOp",EDGE,"E56.right"),sQuery(id+"F26.wireOp",EDGE,"E57.bottom"),sQuery(id+"F26.wireOp",EDGE,"E57.top"),sQuery(id+"F26.wireOp",EDGE,"E57.left"),sQuery(id+"F26.wireOp",EDGE,"E57.right")])],"isStart":false}),makeQuery(id+"F31.opExtrude","CAP_FACE",FACE,{"disambiguationData":[OSD([subQ0]),OD(0.0)],"isStart":false}),makeQuery(id+"F31.opExtrude","CAP_FACE",FACE,{"disambiguationData":[OSD([subQ0]),OD(1.0)],"isStart":false}),makeQuery(id+"F31.opExtrude","CAP_FACE",FACE,{"disambiguationData":[OSD([subQ0]),OD(2.0)],"isStart":false}),makeQuery(id+"F31.opExtrude","CAP_FACE",FACE,{"disambiguationData":[OSD([subQ0]),OD(3.0)],"isStart":false})]});}
            var sketch = newSketch(context, id + "F32", { "sketchPlane" : qUnion([Q0])});
            skLineSegment(sketch, "E102.bottom", {"start": v(92, 67) * mm, "end": v(62, 67) * mm});
            skLineSegment(sketch, "E102.top", {"start": v(92, 37) * mm, "end": v(72, 37) * mm});
            skLineSegment(sketch, "E102.left", {"start": v(92, 67) * mm, "end": v(92, 37) * mm});
            skLineSegment(sketch, "E102.right", {"start": v(62, 67) * mm, "end": v(62, 47) * mm});
            skLineSegment(sketch, "E103.top", {"start": v(62, 47) * mm, "end": v(72, 47) * mm});
            skLineSegment(sketch, "E103.right", {"start": v(72, 37) * mm, "end": v(72, 47) * mm});
            skLineSegment(sketch, "E104.MirrorCS", {"start": v(-62, 67) * mm, "end": v(-62, 47) * mm});
            skLineSegment(sketch, "E105.MirrorCS", {"start": v(-92, 67) * mm, "end": v(-62, 67) * mm});
            skLineSegment(sketch, "E106.MirrorCS", {"start": v(-92, 67) * mm, "end": v(-92, 37) * mm});
            skLineSegment(sketch, "E107.MirrorCS", {"start": v(-92, 37) * mm, "end": v(-72, 37) * mm});
            skLineSegment(sketch, "E108.MirrorCS", {"start": v(-72, 37) * mm, "end": v(-72, 47) * mm});
            skLineSegment(sketch, "E109.MirrorCS", {"start": v(-62, 47) * mm, "end": v(-72, 47) * mm});
            skLineSegment(sketch, "E110.MirrorCS", {"start": v(92, -37) * mm, "end": v(72, -37) * mm});
            skLineSegment(sketch, "E111.MirrorCS", {"start": v(92, -67) * mm, "end": v(92, -37) * mm});
            skLineSegment(sketch, "E112.MirrorCS", {"start": v(92, -67) * mm, "end": v(62, -67) * mm});
            skLineSegment(sketch, "E113.MirrorCS", {"start": v(62, -67) * mm, "end": v(62, -47) * mm});
            skLineSegment(sketch, "E114.MirrorCS", {"start": v(62, -47) * mm, "end": v(72, -47) * mm});
            skLineSegment(sketch, "E115.MirrorCS", {"start": v(72, -37) * mm, "end": v(72, -47) * mm});
            skLineSegment(sketch, "E116.MirrorCS", {"start": v(-62, -67) * mm, "end": v(-62, -47) * mm});
            skLineSegment(sketch, "E117.MirrorCS", {"start": v(-92, -67) * mm, "end": v(-62, -67) * mm});
            skLineSegment(sketch, "E118.MirrorCS", {"start": v(-92, -67) * mm, "end": v(-92, -37) * mm});
            skLineSegment(sketch, "E119.MirrorCS", {"start": v(-92, -37) * mm, "end": v(-72, -37) * mm});
            skLineSegment(sketch, "E120.MirrorCS", {"start": v(-72, -37) * mm, "end": v(-72, -47) * mm});
            skLineSegment(sketch, "E121.MirrorCS", {"start": v(-62, -47) * mm, "end": v(-72, -47) * mm});
            skSolve(sketch);
        }
        {
            var Q0;
            Q0 = qSketchRegion(id + "F32", true);
            extrude(context, id + "F33", {"entities" : qUnion([Q0]), "operationType" : NewBodyOperationType.ADD, "depth" : 2 * mm, "offsetDistance" : 25 * mm});
        }
        {
            var Q0;
            Q0=qCreatedBy(makeId("Top.planeOp"),FACE);
            var sketch = newSketch(context, id + "F34", { "sketchPlane" : qUnion([Q0])});
            skArc(sketch, "E122", {"start": v(-12.46, -1) * mm, "mid": v(0, -12.5) * mm, "end": v(12.46, -1) * mm});
            skLineSegment(sketch, "E123", {"start": v(12.46, -1) * mm, "end": v(23.08, -1) * mm});
            skLineSegment(sketch, "E124", {"start": v(23.08, -1) * mm, "end": v(23.08, -5) * mm});
            skLineSegment(sketch, "E125", {"start": v(23.08, -5) * mm, "end": v(13.08, -5) * mm});
            skLineSegment(sketch, "E126.MirrorCS", {"start": v(-23.08, -5) * mm, "end": v(-13.08, -5) * mm});
            skLineSegment(sketch, "E127.MirrorCS", {"start": v(-23.08, -1) * mm, "end": v(-23.08, -5) * mm});
            skLineSegment(sketch, "E128.MirrorCS", {"start": v(-12.46, -1) * mm, "end": v(-23.08, -1) * mm});
            skArc(sketch, "E129.trimOffspring", {"start": v(-13.08, -5) * mm, "mid": v(0, -14) * mm, "end": v(13.08, -5) * mm});
            skPoint(sketch, "E130.orphan", {"position": v(23.08, 1) * mm});
            skPoint(sketch, "E131.MirrorCS.end.orphan", {"position": v(23.08, 5) * mm});
            skPoint(sketch, "E132.MirrorCS.start.orphan", {"position": v(12.46, 1) * mm});
            skPoint(sketch, "E133.MirrorCS.end.orphan", {"position": v(13.08, 5) * mm});
            skSolve(sketch);
        }
        {
            var Q0;
            Q0 = qSketchRegion(id + "F34", true);
            extrude(context, id + "F35", {"entities" : qUnion([Q0]), "depth" : 10 * mm, "offsetDistance" : 25 * mm});
        }
        {
            var Q0;
            Q0=qCreatedBy(makeId("Top.planeOp"),FACE);
            var sketch = newSketch(context, id + "F36", { "sketchPlane" : qUnion([Q0])});
            skLineSegment(sketch, "E134.bottom", {"start": v(6.57, -14) * mm, "end": v(-15.43, -14) * mm});
            skLineSegment(sketch, "E134.left", {"start": v(6.57, -14) * mm, "end": v(6.57, -29) * mm});
            skLineSegment(sketch, "E134.right", {"start": v(-15.43, -14) * mm, "end": v(-15.43, -29) * mm});
            skLineSegment(sketch, "E135.bottom", {"start": v(11.57, -29) * mm, "end": v(6.57, -29) * mm});
            skLineSegment(sketch, "E135.top", {"start": v(11.57, -32) * mm, "end": v(6.57, -32) * mm});
            skLineSegment(sketch, "E135.left", {"start": v(11.57, -29) * mm, "end": v(11.57, -32) * mm});
            skLineSegment(sketch, "E135.right", {"start": v(-20.43, -29) * mm, "end": v(-20.43, -32) * mm});
            skLineSegment(sketch, "E136.top", {"start": v(6.57, -36) * mm, "end": v(-15.43, -36) * mm});
            skLineSegment(sketch, "E136.left", {"start": v(6.57, -32) * mm, "end": v(6.57, -36) * mm});
            skLineSegment(sketch, "E136.right", {"start": v(-15.43, -32) * mm, "end": v(-15.43, -36) * mm});
            skLineSegment(sketch, "E137.trimOffspring", {"start": v(-15.43, -32) * mm, "end": v(-20.43, -32) * mm});
            skLineSegment(sketch, "E138.trimOffspring", {"start": v(-15.43, -29) * mm, "end": v(-20.43, -29) * mm});
            skSolve(sketch);
        }
        {
            var Q0;
            Q0=makeQuery(id+"F36.imprint","IMPRINT",FACE,{"disambiguationData":[TD([[makeQuery(id+"F36.imprint","IMPRINT",EDGE,{"derivedFrom":sQuery(id+"F36.wireOp",EDGE,"E134.bottom")}),1.0]])]});
            extrude(context, id + "F37", {"entities" : qUnion([Q0]), "depth" : 12 * mm, "offsetDistance" : 25 * mm});
        }
        {
            var Q0;
            Q0=makeQuery(id+"F37.opExtrude","SWEPT_FACE",FACE,{"disambiguationData":[OSD([sQuery(id+"F36.wireOp",EDGE,"E136.top")])]});
            var sketch = newSketch(context, id + "F38", { "sketchPlane" : qUnion([Q0])});
            skCircle(sketch, "E139", {"center": v(-0.94, 5.8) * mm, "radius": 5.1 * mm});
            skSolve(sketch);
        }
        {
            var Q0;
            Q0=makeQuery(id+"F38.imprint","IMPRINT",FACE,{"disambiguationData":[TD([[makeQuery(id+"F38.imprint","IMPRINT",EDGE,{"derivedFrom":sQuery(id+"F38.wireOp",EDGE,"E139")}),1.0]])]});
            extrude(context, id + "F39", {"entities" : qUnion([Q0]), "operationType" : NewBodyOperationType.ADD, "depth" : 5 * mm, "offsetDistance" : 25 * mm});
        }
        {
            var Q0;
            Q0=qCreatedBy(makeId("Top.planeOp"),FACE);
            var sketch = newSketch(context, id + "F40", { "sketchPlane" : qUnion([Q0])});
            skLineSegment(sketch, "E140.bottom", {"start": v(-23.3, -9.35) * mm, "end": v(-38.3, -9.35) * mm});
            skLineSegment(sketch, "E140.top", {"start": v(-23.3, 13.65) * mm, "end": v(-38.3, 13.65) * mm});
            skLineSegment(sketch, "E140.left", {"start": v(-23.3, -9.35) * mm, "end": v(-23.3, 13.65) * mm});
            skLineSegment(sketch, "E141.bottom", {"start": v(-38.3, -14.35) * mm, "end": v(-41.3, -14.35) * mm});
            skLineSegment(sketch, "E141.top", {"start": v(-38.3, 18.65) * mm, "end": v(-41.3, 18.65) * mm});
            skLineSegment(sketch, "E141.left", {"start": v(-38.3, -14.35) * mm, "end": v(-38.3, -9.35) * mm});
            skLineSegment(sketch, "E141.right", {"start": v(-41.3, -14.35) * mm, "end": v(-41.3, -9.35) * mm});
            skLineSegment(sketch, "E142.bottom", {"start": v(-41.3, -9.35) * mm, "end": v(-45.3, -9.35) * mm});
            skLineSegment(sketch, "E142.top", {"start": v(-41.3, 13.65) * mm, "end": v(-45.3, 13.65) * mm});
            skLineSegment(sketch, "E142.right", {"start": v(-45.3, -9.35) * mm, "end": v(-45.3, 13.65) * mm});
            skLineSegment(sketch, "E143.trimOffspring", {"start": v(-38.3, 13.65) * mm, "end": v(-38.3, 18.65) * mm});
            skLineSegment(sketch, "E144.trimOffspring", {"start": v(-41.3, 13.65) * mm, "end": v(-41.3, 18.65) * mm});
            skSolve(sketch);
        }
        {
            var Q0;
            Q0=makeQuery(id+"F40.imprint","IMPRINT",FACE,{"disambiguationData":[TD([[makeQuery(id+"F40.imprint","IMPRINT",EDGE,{"derivedFrom":sQuery(id+"F40.wireOp",EDGE,"E140.bottom")}),-1.0]])]});
            extrude(context, id + "F41", {"entities" : qUnion([Q0]), "depth" : 12 * mm, "offsetDistance" : 25 * mm});
        }
    });
